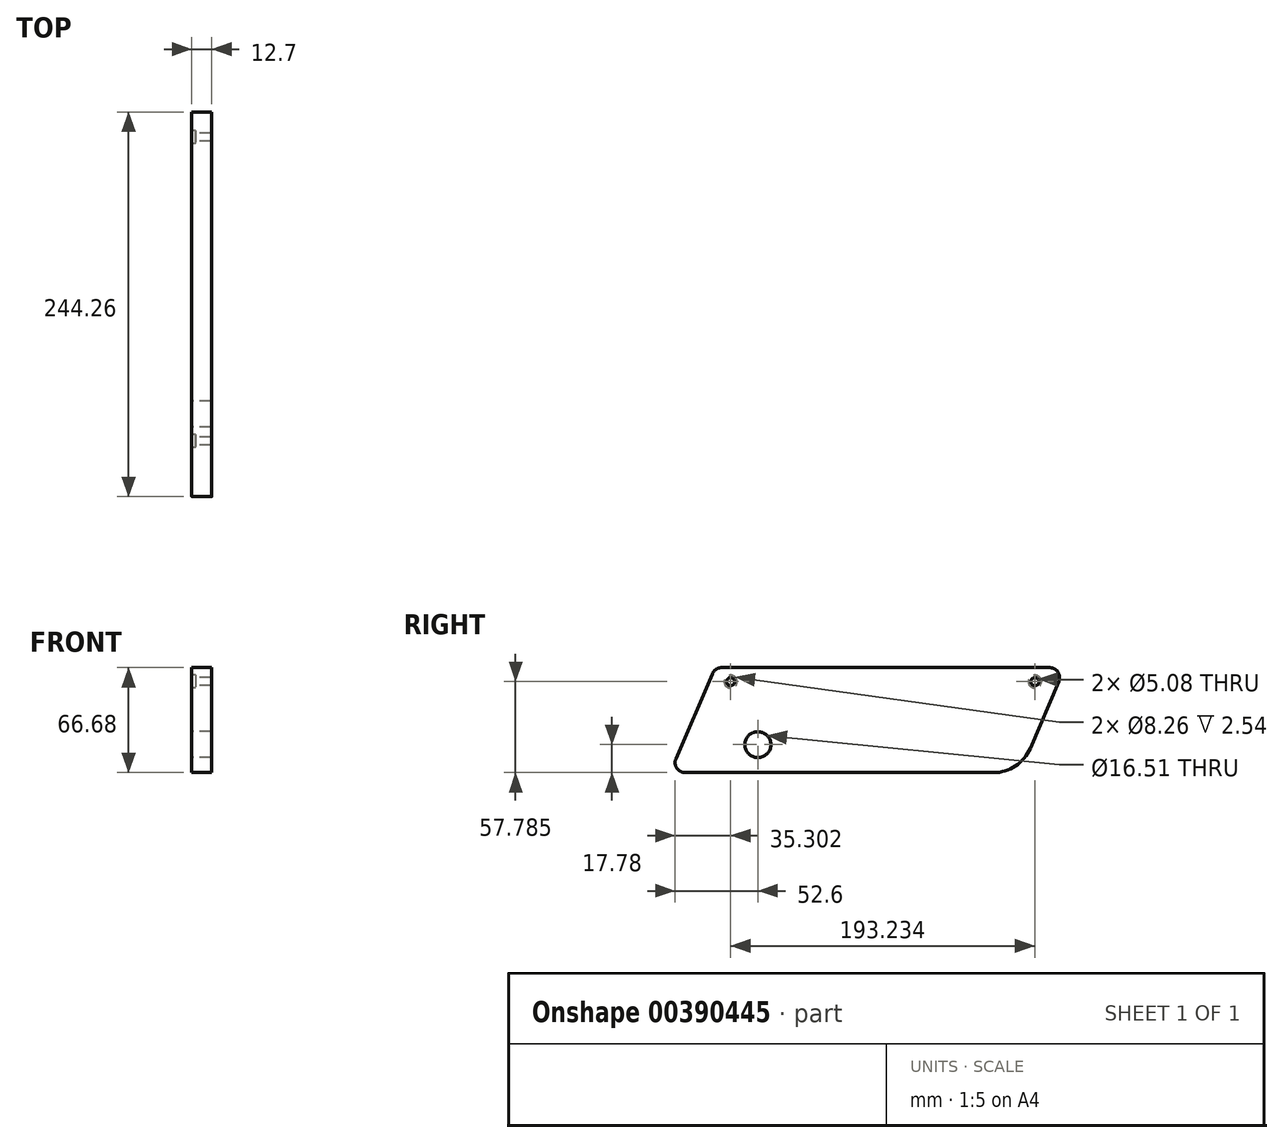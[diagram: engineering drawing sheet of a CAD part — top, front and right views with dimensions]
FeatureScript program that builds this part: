
annotation { "Feature Type Name" : "Feature", "Feature Type Description" : "" }
export const myFeature = defineFeature(function(context is Context, id is Id, definition is map)
    precondition{}
    {
        {
            var Q0;
            Q0=qCreatedBy(makeId("Right.planeOp"),FACE);
            var sketch = newSketch(context, id + "F0", { "sketchPlane" : qUnion([Q0])});
            skCircle(sketch, "E0", {"center": v(0, 0) * mm, "radius": 8.26 * mm});
            skLineSegment(sketch, "E1", {"start": v(-55.88, -17.78) * mm, "end": v(166.37, -17.78) * mm});
            skPoint(sketch, "E2", {"position": v(55.25, -17.78) * mm});
            skLineSegment(sketch, "E3", {"start": v(-27.3, 48.9) * mm, "end": v(194.94, 48.9) * mm});
            skLineSegment(sketch, "E4", {"start": v(-27.3, 48.9) * mm, "end": v(-55.88, -17.78) * mm});
            skLineSegment(sketch, "E5", {"start": v(194.95, 48.9) * mm, "end": v(166.37, -17.78) * mm});
            skSolve(sketch);
        }
        {
            var Q0;
            Q0=makeQuery(id+"F0.imprint","IMPRINT",FACE,{"disambiguationData":[TD([[makeQuery(id+"F0.imprint","IMPRINT",EDGE,{"derivedFrom":sQuery(id+"F0.wireOp",EDGE,"E0")}),-1.0]])]});
            extrude(context, id + "F1", {"entities" : qUnion([Q0]), "depth" : 12.7 * mm});
        }
        {
            var Q0;
            Q0=makeQuery(id+"F1.opExtrude","CAP_FACE",FACE,{"disambiguationData":[OSD([sQuery(id+"F0.wireOp",EDGE,"E0"),sQuery(id+"F0.wireOp",EDGE,"E1"),sQuery(id+"F0.wireOp",EDGE,"E3"),sQuery(id+"F0.wireOp",EDGE,"E4"),sQuery(id+"F0.wireOp",EDGE,"E5")])],"isStart":true});
            var sketch = newSketch(context, id + "F2", { "sketchPlane" : qUnion([Q0])});
            skPoint(sketch, "E6", {"position": v(17.3, 40) * mm});
            skPoint(sketch, "E7", {"position": v(-175.94, 40) * mm});
            skSolve(sketch);
        }
        {
            var Q0;
            Q0=sQuery(id+"F2.wireOp",VERTEX,"E7");
            var Q1;
            Q1=sQuery(id+"F2.wireOp",VERTEX,"E6");
            var Q2;
            Q2=makeQuery(id+"F1.opExtrude","SWEPT_BODY",BODY,{"disambiguationData":[OSD([sQuery(id+"F0.wireOp",EDGE,"E0"),sQuery(id+"F0.wireOp",EDGE,"E1"),sQuery(id+"F0.wireOp",EDGE,"E3"),sQuery(id+"F0.wireOp",EDGE,"E4"),sQuery(id+"F0.wireOp",EDGE,"E5")])]});
            hole(context, id + "F3", {"style" : HoleStyle.C_BORE, "endStyle" : HoleEndStyle.THROUGH, "holeDiameter" : 5.08 * mm, "cBoreDiameter" : 8.25 * mm, "cBoreDepth" : 2.54 * mm, "isTappedThrough" : true, "tappedDepth" : 12.7 * mm, "tapClearance" : 3, "startFromSketch" : true, "locations" : qUnion([Q0, Q1]), "scope" : qUnion([Q2])});
        }
        {
            var Q0;
            Q0=makeQuery(id+"F1.opExtrude","SWEPT_EDGE",EDGE,{"disambiguationData":[OSD([sQuery(id+"F0.wireOp",EDGE,"E3"),sQuery(id+"F0.wireOp",EDGE,"E5")])]});
            var Q1;
            Q1=makeQuery(id+"F1.opExtrude","SWEPT_EDGE",EDGE,{"disambiguationData":[OSD([sQuery(id+"F0.wireOp",EDGE,"E3"),sQuery(id+"F0.wireOp",EDGE,"E4")])]});
            var Q2;
            Q2=makeQuery(id+"F1.opExtrude","SWEPT_EDGE",EDGE,{"disambiguationData":[OSD([sQuery(id+"F0.wireOp",EDGE,"E1"),sQuery(id+"F0.wireOp",EDGE,"E4")])]});
            fillet(context, id + "F4", {"entities" : qUnion([Q0, Q1, Q2]), "radius" : 6.35 * mm, "tangentPropagation" : true, "allowEdgeOverflow" : false});
        }
        {
            var Q0;
            Q0=makeQuery(id+"F1.opExtrude","SWEPT_EDGE",EDGE,{"disambiguationData":[OSD([sQuery(id+"F0.wireOp",EDGE,"E1"),sQuery(id+"F0.wireOp",EDGE,"E5")])]});
            fillet(context, id + "F5", {"entities" : qUnion([Q0]), "radius" : 25.4 * mm, "tangentPropagation" : true, "allowEdgeOverflow" : false});
        }
    });
